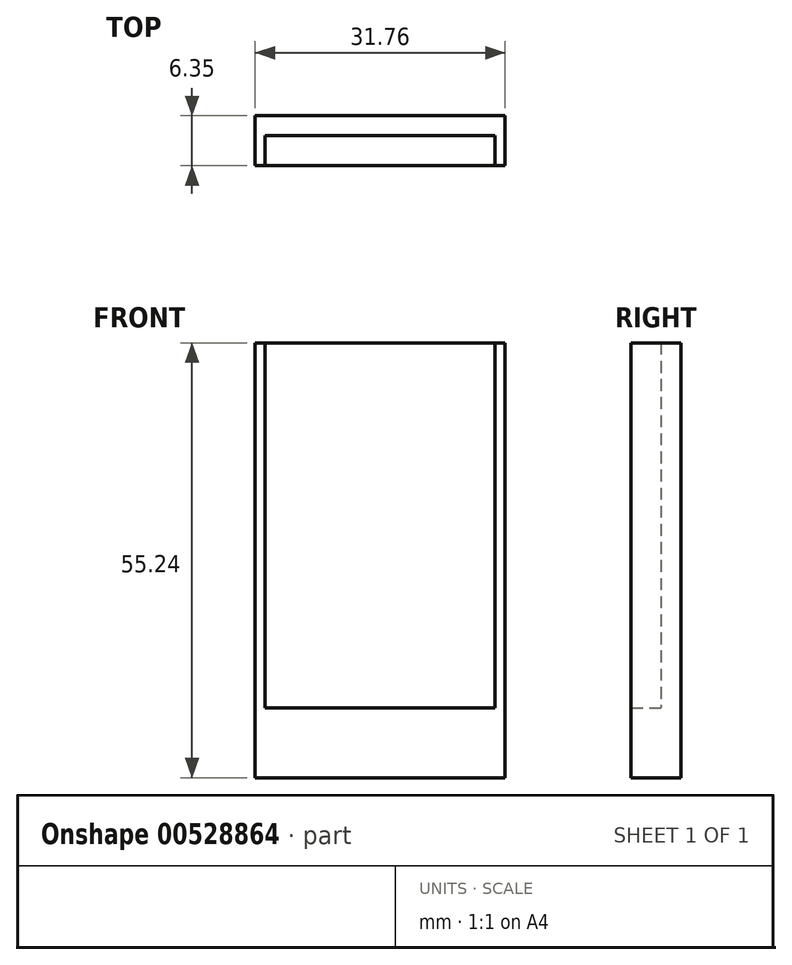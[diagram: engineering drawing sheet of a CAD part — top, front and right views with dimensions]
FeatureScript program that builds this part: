
annotation { "Feature Type Name" : "Feature", "Feature Type Description" : "" }
export const myFeature = defineFeature(function(context is Context, id is Id, definition is map)
    precondition{}
    {
        {
            var Q0;
            Q0=qCreatedBy(makeId("Front.planeOp"),FACE);
            var sketch = newSketch(context, id + "F0", { "sketchPlane" : qUnion([Q0])});
            skLineSegment(sketch, "E0.bottom", {"start": v(15.24, -25.4) * mm, "end": v(-15.24, -25.4) * mm});
            skLineSegment(sketch, "E0.top", {"start": v(15.24, 25.4) * mm, "end": v(-15.24, 25.4) * mm});
            skLineSegment(sketch, "E0.left", {"start": v(15.24, -25.4) * mm, "end": v(15.24, 25.4) * mm});
            skLineSegment(sketch, "E0.right", {"start": v(-15.24, -25.4) * mm, "end": v(-15.24, 25.4) * mm});
            skPoint(sketch, "E0.middle", {"position": v(0, 0) * mm});
            skLineSegment(sketch, "E1.bottom", {"start": v(-15.88, -25.4) * mm, "end": v(-14.6, -25.4) * mm});
            skLineSegment(sketch, "E1.top", {"start": v(-15.87, 25.4) * mm, "end": v(-14.6, 25.4) * mm});
            skLineSegment(sketch, "E1.left", {"start": v(-15.88, -25.4) * mm, "end": v(-15.88, 25.4) * mm});
            skLineSegment(sketch, "E1.right", {"start": v(-14.6, -25.4) * mm, "end": v(-14.6, 25.4) * mm});
            skPoint(sketch, "E1.middle", {"position": v(-15.24, 0) * mm});
            skLineSegment(sketch, "E2.bottom", {"start": v(15.87, -25.4) * mm, "end": v(14.6, -25.4) * mm});
            skLineSegment(sketch, "E2.top", {"start": v(15.88, 25.4) * mm, "end": v(14.6, 25.4) * mm});
            skLineSegment(sketch, "E2.left", {"start": v(15.87, -25.4) * mm, "end": v(15.88, 25.4) * mm});
            skLineSegment(sketch, "E2.right", {"start": v(14.6, -25.4) * mm, "end": v(14.6, 25.4) * mm});
            skPoint(sketch, "E2.middle", {"position": v(15.24, 0) * mm});
            skLineSegment(sketch, "E3.bottom", {"start": v(-15.88, -29.85) * mm, "end": v(15.88, -29.85) * mm});
            skLineSegment(sketch, "E3.top", {"start": v(-15.88, -20.96) * mm, "end": v(15.88, -20.96) * mm});
            skLineSegment(sketch, "E3.left", {"start": v(-15.88, -29.85) * mm, "end": v(-15.88, -20.96) * mm});
            skLineSegment(sketch, "E3.right", {"start": v(15.87, -29.85) * mm, "end": v(15.87, -20.96) * mm});
            skPoint(sketch, "E3.middle", {"position": v(0, -25.4) * mm});
            skSolve(sketch);
        }
        {
            var Q0;
            {var subQ0=sQuery(id+"F0.wireOp",EDGE,"E0.top");Q0=makeQuery(id+"F0.imprint","IMPRINT",FACE,{"disambiguationData":[TD([[makeQuery(id+"F0.imprint","IMPRINT",EDGE,{"derivedFrom":subQ0}),1.0]])]});}
            extrude(context, id + "F1", {"entities" : qUnion([Q0]), "depth" : 2.54 * mm, "offsetDistance" : 25.4 * mm});
        }
        {
            var Q0;
            {var subQ0=sQuery(id+"F0.wireOp",EDGE,"E0.bottom");Q0=makeQuery(id+"F0.imprint","IMPRINT",FACE,{"disambiguationData":[TD([[makeQuery(id+"F0.imprint","IMPRINT",EDGE,{"derivedFrom":subQ0}),-1.0]])]});}
            var Q1;
            {var subQ0=sQuery(id+"F0.wireOp",EDGE,"E2.bottom");var subQ1=sQuery(id+"F0.wireOp",EDGE,"E0.left");var subQ2=makeQuery(id+"F0.imprint","INTERSECT",VERTEX,{"derivedFrom":[subQ1,subQ0]});Q1=makeQuery(id+"F0.imprint","IMPRINT",FACE,{"disambiguationData":[TD([[makeQuery(id+"F0.imprint","IMPRINT",EDGE,{"disambiguationData":[TD([[subQ2,-1.0]])],"derivedFrom":subQ1}),1.0]])]});}
            var Q2;
            {var subQ0=sQuery(id+"F0.wireOp",EDGE,"E1.top");var subQ1=sQuery(id+"F0.wireOp",EDGE,"E0.right");var subQ2=makeQuery(id+"F0.imprint","INTERSECT",VERTEX,{"derivedFrom":[subQ1,subQ0]});Q2=makeQuery(id+"F0.imprint","IMPRINT",FACE,{"disambiguationData":[TD([[makeQuery(id+"F0.imprint","IMPRINT",EDGE,{"disambiguationData":[TD([[subQ2,1.0]])],"derivedFrom":subQ1}),-1.0]])]});}
            var Q3;
            {var subQ5=sQuery(id+"F0.wireOp",EDGE,"E1.left");Q3=makeQuery(id+"F0.imprint","IMPRINT",FACE,{"disambiguationData":[TD([[makeQuery(id+"F0.imprint","IMPRINT",EDGE,{"derivedFrom":subQ5}),-1.0]])]});}
            var Q4;
            {var subQ0=sQuery(id+"F0.wireOp",EDGE,"E1.bottom");var subQ1=sQuery(id+"F0.wireOp",EDGE,"E0.right");var subQ2=makeQuery(id+"F0.imprint","INTERSECT",VERTEX,{"derivedFrom":[subQ1,subQ0]});Q4=makeQuery(id+"F0.imprint","IMPRINT",FACE,{"disambiguationData":[TD([[makeQuery(id+"F0.imprint","IMPRINT",EDGE,{"disambiguationData":[TD([[subQ2,-1.0]])],"derivedFrom":subQ1}),1.0]])]});}
            var Q5;
            {var subQ0=sQuery(id+"F0.wireOp",EDGE,"E1.bottom");var subQ1=sQuery(id+"F0.wireOp",EDGE,"E0.right");var subQ2=makeQuery(id+"F0.imprint","INTERSECT",VERTEX,{"derivedFrom":[subQ1,subQ0]});Q5=makeQuery(id+"F0.imprint","IMPRINT",FACE,{"disambiguationData":[TD([[makeQuery(id+"F0.imprint","IMPRINT",EDGE,{"disambiguationData":[TD([[subQ2,-1.0]])],"derivedFrom":subQ1}),-1.0]])]});}
            var Q6;
            {var subQ5=sQuery(id+"F0.wireOp",EDGE,"E0.bottom");Q6=makeQuery(id+"F0.imprint","IMPRINT",FACE,{"disambiguationData":[TD([[makeQuery(id+"F0.imprint","IMPRINT",EDGE,{"derivedFrom":subQ5}),1.0]])]});}
            var Q7;
            {var subQ0=sQuery(id+"F0.wireOp",EDGE,"E2.bottom");var subQ1=sQuery(id+"F0.wireOp",EDGE,"E0.left");var subQ2=makeQuery(id+"F0.imprint","INTERSECT",VERTEX,{"derivedFrom":[subQ1,subQ0]});Q7=makeQuery(id+"F0.imprint","IMPRINT",FACE,{"disambiguationData":[TD([[makeQuery(id+"F0.imprint","IMPRINT",EDGE,{"disambiguationData":[TD([[subQ2,-1.0]])],"derivedFrom":subQ1}),-1.0]])]});}
            var Q8;
            {var subQ5=sQuery(id+"F0.wireOp",EDGE,"E2.left");Q8=makeQuery(id+"F0.imprint","IMPRINT",FACE,{"disambiguationData":[TD([[makeQuery(id+"F0.imprint","IMPRINT",EDGE,{"derivedFrom":subQ5}),1.0]])]});}
            var Q9;
            {var subQ0=sQuery(id+"F0.wireOp",EDGE,"E2.top");var subQ1=sQuery(id+"F0.wireOp",EDGE,"E0.left");var subQ2=makeQuery(id+"F0.imprint","INTERSECT",VERTEX,{"derivedFrom":[subQ1,subQ0]});Q9=makeQuery(id+"F0.imprint","IMPRINT",FACE,{"disambiguationData":[TD([[makeQuery(id+"F0.imprint","IMPRINT",EDGE,{"disambiguationData":[TD([[subQ2,1.0]])],"derivedFrom":subQ1}),1.0]])]});}
            extrude(context, id + "F2", {"entities" : qUnion([Q0, Q1, Q2, Q3, Q4, Q5, Q6, Q7, Q8, Q9]), "operationType" : NewBodyOperationType.ADD, "depth" : 6.35 * mm, "offsetDistance" : 25.4 * mm});
        }
    });
